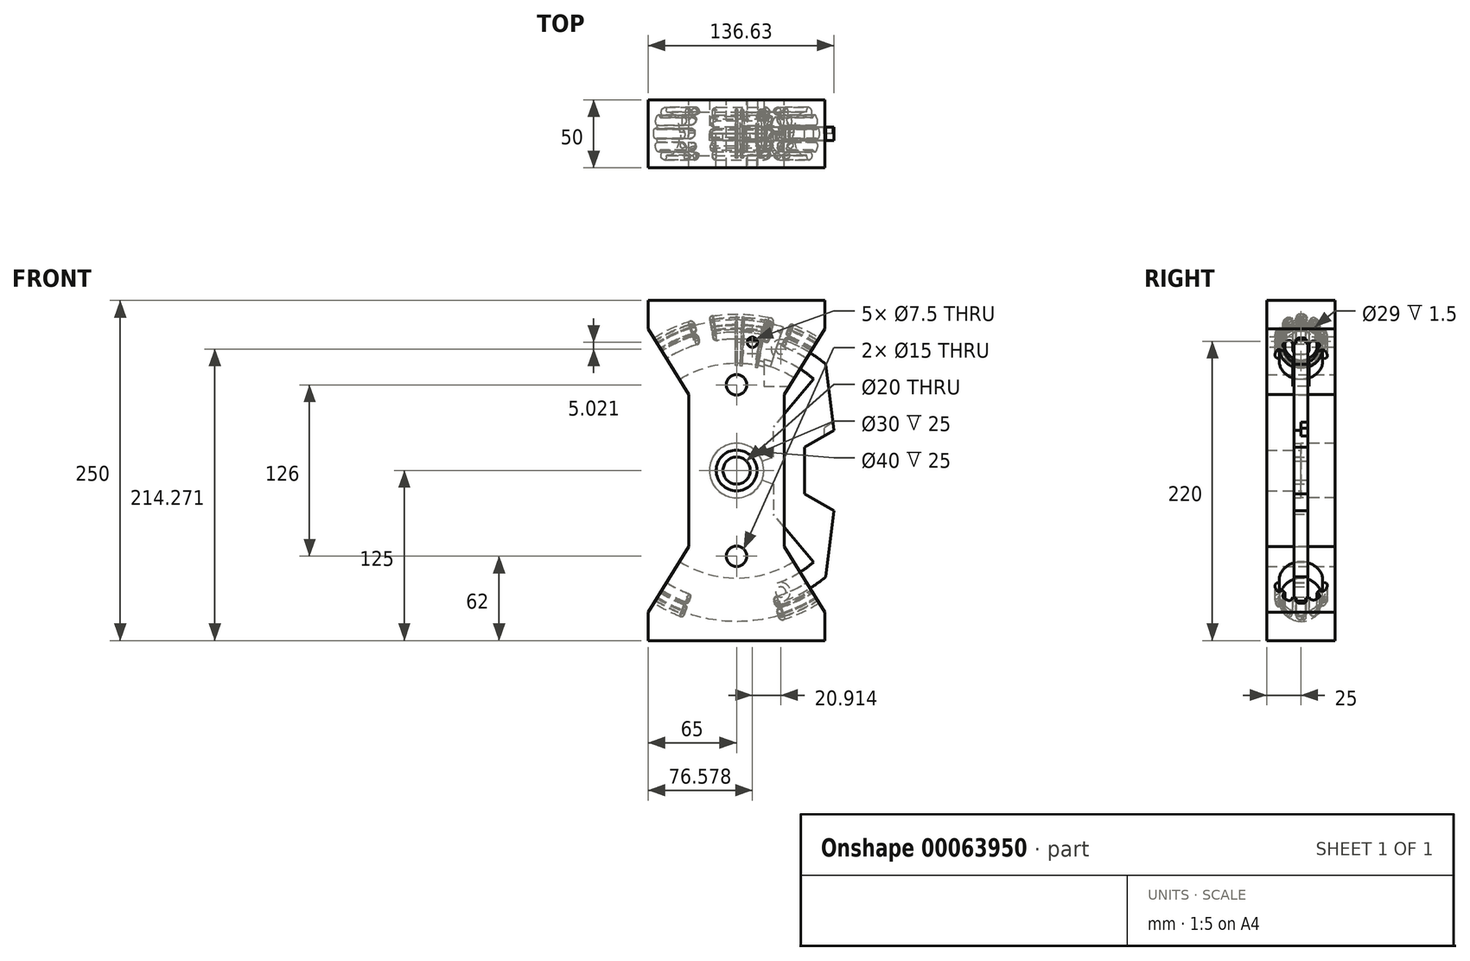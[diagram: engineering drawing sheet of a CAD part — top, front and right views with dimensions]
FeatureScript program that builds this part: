
annotation { "Feature Type Name" : "Feature", "Feature Type Description" : "" }
export const myFeature = defineFeature(function(context is Context, id is Id, definition is map)
    precondition{}
    {
        {
            var Q0;
            Q0=qCreatedBy(makeId("Front.planeOp"),FACE);
            var sketch = newSketch(context, id + "F0", { "sketchPlane" : qUnion([Q0])});
            skCircle(sketch, "E0", {"center": v(0, 0) * mm, "radius": 95 * mm, "construction": true});
            skLineSegment(sketch, "E1", {"start": v(0, 95) * mm, "end": v(0, 0) * mm, "construction": true});
            skLineSegment(sketch, "E2", {"start": v(0, 89.27) * mm, "end": v(32.5, 89.27) * mm, "construction": true});
            skLineSegment(sketch, "E3", {"start": v(0, 0) * mm, "end": v(32.5, 89.27) * mm, "construction": true});
            skLineSegment(sketch, "E4", {"start": v(0, 95) * mm, "end": v(0, 89.27) * mm});
            skLineSegment(sketch, "E5", {"start": v(0, -95) * mm, "end": v(0, -79) * mm});
            skCircle(sketch, "E6", {"center": v(0, 0) * mm, "radius": 79 * mm});
            skLineSegment(sketch, "E7", {"start": v(0, -95) * mm, "end": v(0, -111) * mm});
            skCircle(sketch, "E8", {"center": v(0, 0) * mm, "radius": 111 * mm});
            skLineSegment(sketch, "E9.rect.bottom", {"start": v(65, 125) * mm, "end": v(-65, 125) * mm});
            skLineSegment(sketch, "E9.rect.top", {"start": v(65, -125) * mm, "end": v(-65, -125) * mm});
            skLineSegment(sketch, "E9.rect.left", {"start": v(65, 125) * mm, "end": v(65, -125) * mm});
            skLineSegment(sketch, "E9.rect.right", {"start": v(-65, 125) * mm, "end": v(-65, -125) * mm});
            skCircle(sketch, "E10", {"center": v(0, 0) * mm, "radius": 15 * mm});
            skLineSegment(sketch, "E11", {"start": v(0, 0) * mm, "end": v(65, 104.02) * mm});
            skLineSegment(sketch, "E12", {"start": v(0, 0) * mm, "end": v(143.52, 0) * mm, "construction": true});
            skLineSegment(sketch, "E13", {"start": v(35, 56.01) * mm, "end": v(35, 0) * mm});
            skLineSegment(sketch, "E14", {"start": v(0, 95) * mm, "end": v(32.5, 89.27) * mm, "construction": true});
            skLineSegment(sketch, "E15.MirrorCS", {"start": v(35, -56.01) * mm, "end": v(35, 0) * mm});
            skLineSegment(sketch, "E16.MirrorCS", {"start": v(0, 0) * mm, "end": v(65, -104.02) * mm});
            skLineSegment(sketch, "E17.MirrorCS", {"start": v(0, 0) * mm, "end": v(-65, 104.02) * mm});
            skLineSegment(sketch, "E18.MirrorCS", {"start": v(-35, 56.01) * mm, "end": v(-35, 0) * mm});
            skLineSegment(sketch, "E19.MirrorCS", {"start": v(-35, -56.01) * mm, "end": v(-35, 0) * mm});
            skLineSegment(sketch, "E20.MirrorCS", {"start": v(0, 0) * mm, "end": v(-65, -104.02) * mm});
            skPoint(sketch, "E21", {"position": v(0, 79) * mm});
            skCircle(sketch, "E22", {"center": v(0, 95) * mm, "radius": 16 * mm, "construction": true});
            skLineSegment(sketch, "E23", {"start": v(0, 95) * mm, "end": v(-57.96, 79.47) * mm, "construction": true});
            skLineSegment(sketch, "E24", {"start": v(-14.07, 102.62) * mm, "end": v(-60.8, 90.1) * mm, "construction": true});
            skLineSegment(sketch, "E25", {"start": v(-60.8, 90.1) * mm, "end": v(-57.96, 79.47) * mm, "construction": true});
            skLineSegment(sketch, "E26.MirrorCS", {"start": v(-8.38, 81.37) * mm, "end": v(-55.1, 68.85) * mm, "construction": true});
            skLineSegment(sketch, "E27.MirrorCS", {"start": v(-55.1, 68.85) * mm, "end": v(-57.96, 79.47) * mm, "construction": true});
            skCircle(sketch, "E28", {"center": v(0, 63) * mm, "radius": 7.5 * mm});
            skCircle(sketch, "E29.MirrorC", {"center": v(0, -63) * mm, "radius": 7.5 * mm});
            skSolve(sketch);
        }
        {
            var Q0;
            {var subQ1=sQuery(id+"F0.wireOp",EDGE,"E9.rect.bottom");Q0=makeQuery(id+"F0.imprint","IMPRINT",FACE,{"disambiguationData":[TD([[makeQuery(id+"F0.imprint","IMPRINT",EDGE,{"derivedFrom":subQ1}),1.0]])]});}
            var Q1;
            {var subQ1=sQuery(id+"F0.wireOp",EDGE,"E9.rect.top");Q1=makeQuery(id+"F0.imprint","IMPRINT",FACE,{"disambiguationData":[TD([[makeQuery(id+"F0.imprint","IMPRINT",EDGE,{"derivedFrom":subQ1}),-1.0]])]});}
            var Q2;
            {var subQ0=sQuery(id+"F0.wireOp",EDGE,"E11");var subQ1=sQuery(id+"F0.wireOp",EDGE,"E6");var subQ2=makeQuery(id+"F0.imprint","INTERSECT",VERTEX,{"derivedFrom":[subQ1,subQ0]});Q2=makeQuery(id+"F0.imprint","IMPRINT",FACE,{"disambiguationData":[TD([[makeQuery(id+"F0.imprint","IMPRINT",EDGE,{"disambiguationData":[TD([[subQ2,-1.0]])],"derivedFrom":subQ1}),-1.0]])]});}
            var Q3;
            {var subQ0=sQuery(id+"F0.wireOp",EDGE,"E11");var subQ2=sQuery(id+"F0.wireOp",EDGE,"E6");var subQ3=makeQuery(id+"F0.imprint","INTERSECT",VERTEX,{"derivedFrom":[subQ2,subQ0]});Q3=makeQuery(id+"F0.imprint","IMPRINT",FACE,{"disambiguationData":[TD([[makeQuery(id+"F0.imprint","IMPRINT",EDGE,{"disambiguationData":[TD([[subQ3,-1.0]])],"derivedFrom":subQ2}),1.0]])]});}
            var Q4;
            {var subQ1=sQuery(id+"F0.wireOp",EDGE,"E18.MirrorCS");Q4=makeQuery(id+"F0.imprint","IMPRINT",FACE,{"disambiguationData":[TD([[makeQuery(id+"F0.imprint","IMPRINT",EDGE,{"derivedFrom":subQ1}),1.0]])]});}
            var Q5;
            {var subQ1=sQuery(id+"F0.wireOp",EDGE,"E13");Q5=makeQuery(id+"F0.imprint","IMPRINT",FACE,{"disambiguationData":[TD([[makeQuery(id+"F0.imprint","IMPRINT",EDGE,{"derivedFrom":subQ1}),-1.0]])]});}
            var Q6;
            {var subQ2=sQuery(id+"F0.wireOp",EDGE,"E5");Q6=makeQuery(id+"F0.imprint","IMPRINT",FACE,{"disambiguationData":[TD([[makeQuery(id+"F0.imprint","IMPRINT",EDGE,{"derivedFrom":subQ2}),-1.0]])]});}
            var Q7;
            {var subQ2=sQuery(id+"F0.wireOp",EDGE,"E5");Q7=makeQuery(id+"F0.imprint","IMPRINT",FACE,{"disambiguationData":[TD([[makeQuery(id+"F0.imprint","IMPRINT",EDGE,{"derivedFrom":subQ2}),1.0]])]});}
            var Q8;
            {var subQ6=sQuery(id+"F0.wireOp",EDGE,"E6");var subQ7=makeQuery(id+"F0.imprint","INTERSECT",VERTEX,{"derivedFrom":[sQuery(id+"F0.wireOp",EDGE,"E5"),subQ6]});Q8=makeQuery(id+"F0.imprint","IMPRINT",FACE,{"disambiguationData":[TD([[makeQuery(id+"F0.imprint","IMPRINT",EDGE,{"disambiguationData":[TD([[subQ7,1.0]])],"derivedFrom":subQ6}),1.0]])]});}
            extrude(context, id + "F1", {"entities" : qUnion([Q0, Q1, Q2, Q3, Q4, Q5, Q6, Q7, Q8]), "endBound" : BoundingType.SYMMETRIC, "depth" : 50 * mm});
        }
        {
            var Q0;
            Q0=qCreatedBy(makeId("Right.planeOp"),FACE);
            var sketch = newSketch(context, id + "F2", { "sketchPlane" : qUnion([Q0])});
            skCircle(sketch, "E30", {"center": v(0, 95) * mm, "radius": 16 * mm});
            skLineSegment(sketch, "E31", {"start": v(-6, 80.17) * mm, "end": v(-6, 0) * mm});
            skLineSegment(sketch, "E32", {"start": v(-6, 0) * mm, "end": v(0, 0) * mm});
            skLineSegment(sketch, "E33", {"start": v(0, 0) * mm, "end": v(6, 0) * mm});
            skLineSegment(sketch, "E34", {"start": v(6, 0) * mm, "end": v(6, 80.17) * mm});
            skLineSegment(sketch, "E35", {"start": v(-6, 0) * mm, "end": v(-85.58, 0) * mm});
            skSolve(sketch);
        }
        {
            var Q0;
            {var subQ0=sQuery(id+"F2.wireOp",EDGE,"E30");var subQ1=makeQuery(id+"F2.imprint","INTERSECT",VERTEX,{"derivedFrom":[subQ0,sQuery(id+"F2.wireOp",EDGE,"E31")]});Q0=makeQuery(id+"F2.imprint","IMPRINT",FACE,{"disambiguationData":[TD([[makeQuery(id+"F2.imprint","IMPRINT",EDGE,{"disambiguationData":[TD([[subQ1,-1.0]])],"derivedFrom":subQ0}),1.0]])]});}
            var Q1;
            Q1=sQuery(id+"F2.wireOp",EDGE,"E35");
            revolve(context, id + "F3", {"operationType" : NewBodyOperationType.REMOVE, "entities" : qUnion([Q0]), "axis" : qUnion([Q1]), "revolveType" : RevolveType.FULL, "oppositeDirection" : true});
        }
        {
            var Q0;
            Q0=qCreatedBy(makeId("Right.planeOp"),FACE);
            var sketch = newSketch(context, id + "F4", { "sketchPlane" : qUnion([Q0])});
            skCircle(sketch, "E36", {"center": v(0, 95) * mm, "radius": 15.98 * mm});
            skSolve(sketch);
        }
        {
            var Q0;
            Q0=qSketchRegion(id+"F4",true);
            var Q1;
            Q1=sQuery(id+"F2.wireOp",EDGE,"E35");
            revolve(context, id + "F5", {"entities" : qUnion([Q0]), "axis" : qUnion([Q1]), "revolveType" : RevolveType.ONE_DIRECTION, "oppositeDirection" : true, "angle" : 18 * degree});
        }
        {
            var Q0;
            Q0=qCreatedBy(makeId("Front.planeOp"),FACE);
            var sketch = newSketch(context, id + "F6", { "sketchPlane" : qUnion([Q0])});
            skLineSegment(sketch, "E37", {"start": v(0, 0) * mm, "end": v(0, 138.47) * mm});
            skLineSegment(sketch, "E38", {"start": v(0, 0) * mm, "end": v(11.58, 94.3) * mm});
            skCircle(sketch, "E39", {"center": v(11.58, 94.3) * mm, "radius": 3.75 * mm});
            skLineSegment(sketch, "E40", {"start": v(0, 0) * mm, "end": v(37.76, 116.21) * mm});
            skCircle(sketch, "E41", {"center": v(11.58, 94.3) * mm, "radius": 6.14 * mm});
            skLineSegment(sketch, "E42.bottom", {"start": v(20.13, 102.54) * mm, "end": v(41.82, 102.54) * mm});
            skLineSegment(sketch, "E42.top", {"start": v(20.13, 61.74) * mm, "end": v(41.82, 61.74) * mm});
            skLineSegment(sketch, "E42.left", {"start": v(20.13, 102.54) * mm, "end": v(20.13, 61.74) * mm});
            skLineSegment(sketch, "E42.right", {"start": v(41.82, 102.54) * mm, "end": v(41.82, 61.74) * mm});
            skLineSegment(sketch, "E43.bottom", {"start": v(20.13, 102.54) * mm, "end": v(5.32, 102.54) * mm});
            skLineSegment(sketch, "E43.top", {"start": v(20.13, 85.67) * mm, "end": v(5.32, 85.67) * mm});
            skLineSegment(sketch, "E43.left", {"start": v(20.13, 102.54) * mm, "end": v(20.13, 85.67) * mm});
            skLineSegment(sketch, "E43.right", {"start": v(5.32, 102.54) * mm, "end": v(5.32, 85.67) * mm});
            skSolve(sketch);
        }
        {
            var Q0;
            {var subQ5=sQuery(id+"F6.wireOp",EDGE,"E42.right");Q0=makeQuery(id+"F6.imprint","IMPRINT",FACE,{"disambiguationData":[TD([[makeQuery(id+"F6.imprint","IMPRINT",EDGE,{"derivedFrom":subQ5}),-1.0]])]});}
            var Q1;
            {var subQ0=sQuery(id+"F6.wireOp",EDGE,"E42.left");Q1=makeQuery(id+"F6.imprint","IMPRINT",FACE,{"disambiguationData":[TD([[makeQuery(id+"F6.imprint","IMPRINT",EDGE,{"derivedFrom":subQ0}),1.0]])]});}
            var Q2;
            Q2=makeQuery(id+"F6.imprint","IMPRINT",FACE,{"disambiguationData":[TD([[makeQuery(id+"F6.imprint","IMPRINT",EDGE,{"derivedFrom":sQuery(id+"F6.wireOp",EDGE,"E41")}),-1.0]])]});
            var Q3;
            Q3=makeQuery(id+"F6.imprint","IMPRINT",FACE,{"disambiguationData":[TD([[makeQuery(id+"F6.imprint","IMPRINT",EDGE,{"derivedFrom":sQuery(id+"F6.wireOp",EDGE,"E39")}),-1.0]])]});
            var Q4;
            Q4=makeQuery(id+"F6.imprint","IMPRINT",FACE,{"disambiguationData":[TD([[makeQuery(id+"F6.imprint","IMPRINT",EDGE,{"derivedFrom":sQuery(id+"F6.wireOp",EDGE,"E39")}),1.0]])]});
            extrude(context, id + "F7", {"entities" : qUnion([Q0, Q1, Q2, Q3, Q4]), "operationType" : NewBodyOperationType.REMOVE, "endBound" : BoundingType.SYMMETRIC, "oppositeDirection" : true, "depth" : 12 * mm});
        }
        {
            var Q0;
            Q0=makeQuery(id+"F7.boolean.opBoolean","COPY",EDGE,{"derivedFrom":makeQuery(id+"F7.opExtrude","CAP_EDGE",EDGE,{"disambiguationData":[OSD([sQuery(id+"F6.wireOp",EDGE,"E42.bottom"),sQuery(id+"F6.wireOp",EDGE,"E43.bottom")])],"isStart":false})});
            var Q1;
            Q1=makeQuery(id+"F7.boolean.opBoolean","COPY",EDGE,{"derivedFrom":makeQuery(id+"F7.opExtrude","CAP_EDGE",EDGE,{"disambiguationData":[OSD([sQuery(id+"F6.wireOp",EDGE,"E42.bottom"),sQuery(id+"F6.wireOp",EDGE,"E43.bottom")])],"isStart":true})});
            var Q2;
            Q2=makeQuery(id+"F7.boolean.opBoolean","COPY",EDGE,{"derivedFrom":makeQuery(id+"F7.opExtrude","CAP_EDGE",EDGE,{"disambiguationData":[OSD([sQuery(id+"F6.wireOp",EDGE,"E43.top")])],"isStart":false})});
            var Q3;
            Q3=makeQuery(id+"F7.boolean.opBoolean","COPY",EDGE,{"derivedFrom":makeQuery(id+"F7.opExtrude","CAP_EDGE",EDGE,{"disambiguationData":[OSD([sQuery(id+"F6.wireOp",EDGE,"E43.top")])],"isStart":true})});
            fillet(context, id + "F8", {"entities" : qUnion([Q0, Q1, Q2, Q3]), "radius" : 3 * mm, "allowEdgeOverflow" : false});
        }
        {
            var Q0;
            Q0=makeQuery(id+"F6.imprint","IMPRINT",FACE,{"disambiguationData":[TD([[makeQuery(id+"F6.imprint","IMPRINT",EDGE,{"derivedFrom":sQuery(id+"F6.wireOp",EDGE,"E39")}),1.0]])]});
            extrude(context, id + "F9", {"entities" : qUnion([Q0]), "operationType" : NewBodyOperationType.REMOVE, "endBound" : BoundingType.SYMMETRIC, "oppositeDirection" : true, "depth" : 50 * mm});
        }
        {
            var Q0;
            Q0=qCreatedBy(makeId("Right.planeOp"),FACE);
            var sketch = newSketch(context, id + "F10", { "sketchPlane" : qUnion([Q0])});
            skCircle(sketch, "E44", {"center": v(0, 95) * mm, "radius": 12.5 * mm});
            skSolve(sketch);
        }
        {
            var Q0;
            Q0=qSketchRegion(id+"F10",true);
            var Q1;
            Q1=sQuery(id+"F2.wireOp",EDGE,"E35");
            revolve(context, id + "F11", {"operationType" : NewBodyOperationType.REMOVE, "entities" : qUnion([Q0]), "axis" : qUnion([Q1]), "revolveType" : RevolveType.TWO_DIRECTIONS, "oppositeDirection" : true, "angle" : 30 * degree, "angleBack" : 10 * degree});
        }
        {
            var Q0;
            Q0=qCreatedBy(makeId("Right.planeOp"),FACE);
            var sketch = newSketch(context, id + "F12", { "sketchPlane" : qUnion([Q0])});
            skCircle(sketch, "E45", {"center": v(0, 95) * mm, "radius": 14.5 * mm});
            skCircle(sketch, "E46", {"center": v(0, 95) * mm, "radius": 18 * mm});
            skSolve(sketch);
        }
        {
            var Q0;
            Q0=qSketchRegion(id+"F12",true);
            extrude(context, id + "F13", {"entities" : qUnion([Q0]), "endBound" : BoundingType.SYMMETRIC, "depth" : 1.5 * mm});
        }
        {
            var Q0;
            Q0=makeQuery(id+"F13.opExtrude","SWEPT_BODY",BODY,{"disambiguationData":[OSD([sQuery(id+"F12.wireOp",EDGE,"E45"),sQuery(id+"F12.wireOp",EDGE,"E46")])]});
            var Q1;
            Q1=sQuery(id+"F2.wireOp",EDGE,"E35");
            transform(context, id + "F14", {"entities" : qUnion([Q0]), "transformType" : TransformType.ROTATION, "transformAxis" : qUnion([Q1]), "angle" : 2.5 * degree, "oppositeDirection" : true, "makeCopy" : true});
        }
        {
            var Q0;
            Q0=makeQuery(id+"F13.opExtrude","SWEPT_BODY",BODY,{"disambiguationData":[OSD([sQuery(id+"F12.wireOp",EDGE,"E45"),sQuery(id+"F12.wireOp",EDGE,"E46")])]});
            var Q1;
            Q1=sQuery(id+"F2.wireOp",EDGE,"E35");
            transform(context, id + "F15", {"entities" : qUnion([Q0]), "transformType" : TransformType.ROTATION, "transformAxis" : qUnion([Q1]), "angle" : 11 * degree, "oppositeDirection" : true, "makeCopy" : true});
        }
        {
            var Q0;
            Q0=makeQuery(id+"F14.opPattern","COPY",BODY,{"derivedFrom":makeQuery(id+"F13.opExtrude","SWEPT_BODY",BODY,{"disambiguationData":[OSD([sQuery(id+"F12.wireOp",EDGE,"E45"),sQuery(id+"F12.wireOp",EDGE,"E46")])]}),"instanceName":"1"});
            var Q1;
            Q1=makeQuery(id+"F15.opPattern","COPY",BODY,{"derivedFrom":makeQuery(id+"F13.opExtrude","SWEPT_BODY",BODY,{"disambiguationData":[OSD([sQuery(id+"F12.wireOp",EDGE,"E45"),sQuery(id+"F12.wireOp",EDGE,"E46")])]}),"instanceName":"1"});
            var Q2;
            Q2=makeQuery(id+"F5.opRevolve","SWEPT_BODY",BODY,{"disambiguationData":[OSD([sQuery(id+"F4.wireOp",EDGE,"E36")])]});
            booleanBodies(context, id + "F16", {"operationType" : BooleanOperationType.SUBTRACTION, "tools" : qUnion([Q0, Q1]), "targets" : qUnion([Q2]), "keepTools" : true});
        }
        {
            var Q0;
            Q0=qCreatedBy(makeId("Front.planeOp"),FACE);
            var sketch = newSketch(context, id + "F17", { "sketchPlane" : qUnion([Q0])});
            skCircle(sketch, "E47", {"center": v(0, 0) * mm, "radius": 20 * mm});
            skLineSegment(sketch, "E48", {"start": v(0, 0) * mm, "end": v(27, 9.83) * mm});
            skLineSegment(sketch, "E49", {"start": v(0, 0) * mm, "end": v(-52.85, 0) * mm});
            skLineSegment(sketch, "E50", {"start": v(0, 0) * mm, "end": v(32.5, 89.27) * mm, "construction": true});
            skCircle(sketch, "E51", {"center": v(32.5, 89.27) * mm, "radius": 7 * mm});
            skCircle(sketch, "E52", {"center": v(32.5, 89.27) * mm, "radius": 3.75 * mm});
            skArc(sketch, "E53", {"start": v(56.57, 67.41) * mm, "mid": v(44, 76.21) * mm, "end": v(30.1, 82.7) * mm});
            skArc(sketch, "E54", {"start": v(65.56, 78.14) * mm, "mid": v(51, 88.33) * mm, "end": v(34.89, 95.85) * mm});
            skLineSegment(sketch, "E55", {"start": v(56.57, 67.41) * mm, "end": v(0, 0) * mm});
            skLineSegment(sketch, "E56", {"start": v(56.57, 67.41) * mm, "end": v(65.56, 78.14) * mm});
            skLineSegment(sketch, "E57", {"start": v(27, 9.83) * mm, "end": v(27, 32.18) * mm});
            skLineSegment(sketch, "E58", {"start": v(65.56, 78.14) * mm, "end": v(71.63, 29.58) * mm});
            skLineSegment(sketch, "E59", {"start": v(71.63, 29.58) * mm, "end": v(50, 17.1) * mm});
            skLineSegment(sketch, "E60", {"start": v(50, 17.1) * mm, "end": v(50, 0) * mm});
            skLineSegment(sketch, "E61.MirrorCS", {"start": v(0, 0) * mm, "end": v(32.5, -89.27) * mm, "construction": true});
            skLineSegment(sketch, "E62.MirrorCS", {"start": v(56.57, -67.41) * mm, "end": v(0, 0) * mm});
            skArc(sketch, "E63.MirrorCS", {"start": v(56.57, -67.41) * mm, "mid": v(44, -76.21) * mm, "end": v(30.1, -82.7) * mm});
            skCircle(sketch, "E64.MirrorC", {"center": v(32.5, -89.27) * mm, "radius": 7 * mm});
            skCircle(sketch, "E65.MirrorC", {"center": v(32.5, -89.27) * mm, "radius": 3.75 * mm});
            skArc(sketch, "E66.MirrorCS", {"start": v(65.56, -78.14) * mm, "mid": v(51, -88.33) * mm, "end": v(34.89, -95.85) * mm});
            skLineSegment(sketch, "E67.MirrorCS", {"start": v(65.56, -78.14) * mm, "end": v(71.63, -29.58) * mm});
            skLineSegment(sketch, "E68.MirrorCS", {"start": v(71.63, -29.58) * mm, "end": v(50, -17.1) * mm});
            skLineSegment(sketch, "E69.MirrorCS", {"start": v(50, -17.1) * mm, "end": v(50, 0) * mm});
            skLineSegment(sketch, "E70.MirrorCS", {"start": v(27, -9.83) * mm, "end": v(27, -32.18) * mm});
            skLineSegment(sketch, "E71.MirrorCS", {"start": v(0, 0) * mm, "end": v(27, -9.83) * mm});
            skCircle(sketch, "E72", {"center": v(0, 0) * mm, "radius": 10 * mm});
            skSolve(sketch);
        }
        {
            var Q0;
            Q0=makeQuery(id+"F17.imprint","IMPRINT",FACE,{"disambiguationData":[TD([[makeQuery(id+"F17.imprint","IMPRINT",EDGE,{"derivedFrom":sQuery(id+"F17.wireOp",EDGE,"E52")}),-1.0]])]});
            var Q1;
            {var subQ0=sQuery(id+"F17.wireOp",EDGE,"E53");Q1=makeQuery(id+"F17.imprint","IMPRINT",FACE,{"disambiguationData":[TD([[makeQuery(id+"F17.imprint","IMPRINT",EDGE,{"derivedFrom":subQ0}),-1.0]])]});}
            var Q2;
            {var subQ9=sQuery(id+"F17.wireOp",EDGE,"E56");Q2=makeQuery(id+"F17.imprint","IMPRINT",FACE,{"disambiguationData":[TD([[makeQuery(id+"F17.imprint","IMPRINT",EDGE,{"derivedFrom":subQ9}),-1.0]])]});}
            var Q3;
            {var subQ0=sQuery(id+"F17.wireOp",EDGE,"E48");var subQ1=sQuery(id+"F17.wireOp",EDGE,"E47");var subQ2=makeQuery(id+"F17.imprint","INTERSECT",VERTEX,{"derivedFrom":[subQ1,subQ0]});Q3=makeQuery(id+"F17.imprint","IMPRINT",FACE,{"disambiguationData":[TD([[makeQuery(id+"F17.imprint","IMPRINT",EDGE,{"disambiguationData":[TD([[subQ2,1.0]])],"derivedFrom":subQ1}),1.0]])]});}
            var Q4;
            {var subQ0=sQuery(id+"F17.wireOp",EDGE,"E49");var subQ1=sQuery(id+"F17.wireOp",EDGE,"E47");var subQ2=makeQuery(id+"F17.imprint","INTERSECT",VERTEX,{"derivedFrom":[subQ1,subQ0]});Q4=makeQuery(id+"F17.imprint","IMPRINT",FACE,{"disambiguationData":[TD([[makeQuery(id+"F17.imprint","IMPRINT",EDGE,{"disambiguationData":[TD([[subQ2,1.0]])],"derivedFrom":subQ1}),1.0]])]});}
            var Q5;
            {var subQ0=sQuery(id+"F17.wireOp",EDGE,"E55");var subQ1=sQuery(id+"F17.wireOp",EDGE,"E47");var subQ2=makeQuery(id+"F17.imprint","INTERSECT",VERTEX,{"derivedFrom":[subQ1,subQ0]});Q5=makeQuery(id+"F17.imprint","IMPRINT",FACE,{"disambiguationData":[TD([[makeQuery(id+"F17.imprint","IMPRINT",EDGE,{"disambiguationData":[TD([[subQ2,1.0]])],"derivedFrom":subQ1}),1.0]])]});}
            var Q6;
            {var subQ0=sQuery(id+"F17.wireOp",EDGE,"E62.MirrorCS");var subQ1=sQuery(id+"F17.wireOp",EDGE,"E47");var subQ2=makeQuery(id+"F17.imprint","INTERSECT",VERTEX,{"derivedFrom":[subQ1,subQ0]});Q6=makeQuery(id+"F17.imprint","IMPRINT",FACE,{"disambiguationData":[TD([[makeQuery(id+"F17.imprint","IMPRINT",EDGE,{"disambiguationData":[TD([[subQ2,-1.0]])],"derivedFrom":subQ1}),1.0]])]});}
            var Q7;
            {var subQ0=sQuery(id+"F17.wireOp",EDGE,"E49");var subQ1=sQuery(id+"F17.wireOp",EDGE,"E47");var subQ2=makeQuery(id+"F17.imprint","INTERSECT",VERTEX,{"derivedFrom":[subQ1,subQ0]});Q7=makeQuery(id+"F17.imprint","IMPRINT",FACE,{"disambiguationData":[TD([[makeQuery(id+"F17.imprint","IMPRINT",EDGE,{"disambiguationData":[TD([[subQ2,-1.0]])],"derivedFrom":subQ1}),1.0]])]});}
            var Q8;
            Q8=makeQuery(id+"F17.imprint","IMPRINT",FACE,{"disambiguationData":[TD([[makeQuery(id+"F17.imprint","IMPRINT",EDGE,{"derivedFrom":sQuery(id+"F17.wireOp",EDGE,"E65.MirrorC")}),1.0]])]});
            extrude(context, id + "F18", {"entities" : qUnion([Q0, Q1, Q2, Q3, Q4, Q5, Q6, Q7, Q8]), "endBound" : BoundingType.SYMMETRIC, "depth" : 10 * mm});
        }
        {
            var Q0;
            {var subQ0=sQuery(id+"F17.wireOp",EDGE,"E49");var subQ1=sQuery(id+"F17.wireOp",EDGE,"E47");var subQ2=makeQuery(id+"F17.imprint","INTERSECT",VERTEX,{"derivedFrom":[subQ1,subQ0]});Q0=makeQuery(id+"F17.imprint","IMPRINT",FACE,{"disambiguationData":[TD([[makeQuery(id+"F17.imprint","IMPRINT",EDGE,{"disambiguationData":[TD([[subQ2,1.0]])],"derivedFrom":subQ1}),1.0]])]});}
            var Q1;
            {var subQ0=sQuery(id+"F17.wireOp",EDGE,"E55");var subQ1=sQuery(id+"F17.wireOp",EDGE,"E47");var subQ2=makeQuery(id+"F17.imprint","INTERSECT",VERTEX,{"derivedFrom":[subQ1,subQ0]});Q1=makeQuery(id+"F17.imprint","IMPRINT",FACE,{"disambiguationData":[TD([[makeQuery(id+"F17.imprint","IMPRINT",EDGE,{"disambiguationData":[TD([[subQ2,1.0]])],"derivedFrom":subQ1}),1.0]])]});}
            var Q2;
            {var subQ0=sQuery(id+"F17.wireOp",EDGE,"E48");var subQ1=sQuery(id+"F17.wireOp",EDGE,"E47");var subQ2=makeQuery(id+"F17.imprint","INTERSECT",VERTEX,{"derivedFrom":[subQ1,subQ0]});Q2=makeQuery(id+"F17.imprint","IMPRINT",FACE,{"disambiguationData":[TD([[makeQuery(id+"F17.imprint","IMPRINT",EDGE,{"disambiguationData":[TD([[subQ2,1.0]])],"derivedFrom":subQ1}),1.0]])]});}
            var Q3;
            {var subQ0=sQuery(id+"F17.wireOp",EDGE,"E62.MirrorCS");var subQ1=sQuery(id+"F17.wireOp",EDGE,"E47");var subQ2=makeQuery(id+"F17.imprint","INTERSECT",VERTEX,{"derivedFrom":[subQ1,subQ0]});Q3=makeQuery(id+"F17.imprint","IMPRINT",FACE,{"disambiguationData":[TD([[makeQuery(id+"F17.imprint","IMPRINT",EDGE,{"disambiguationData":[TD([[subQ2,-1.0]])],"derivedFrom":subQ1}),1.0]])]});}
            var Q4;
            {var subQ0=sQuery(id+"F17.wireOp",EDGE,"E49");var subQ1=sQuery(id+"F17.wireOp",EDGE,"E47");var subQ2=makeQuery(id+"F17.imprint","INTERSECT",VERTEX,{"derivedFrom":[subQ1,subQ0]});Q4=makeQuery(id+"F17.imprint","IMPRINT",FACE,{"disambiguationData":[TD([[makeQuery(id+"F17.imprint","IMPRINT",EDGE,{"disambiguationData":[TD([[subQ2,-1.0]])],"derivedFrom":subQ1}),1.0]])]});}
            extrude(context, id + "F19", {"entities" : qUnion([Q0, Q1, Q2, Q3, Q4]), "operationType" : NewBodyOperationType.REMOVE, "oppositeDirection" : true, "depth" : 25 * mm});
        }
        {
            var Q0;
            Q0=qCreatedBy(makeId("Right.planeOp"),FACE);
            var sketch = newSketch(context, id + "F20", { "sketchPlane" : qUnion([Q0])});
            skCircle(sketch, "E73", {"center": v(0, 95) * mm, "radius": 20 * mm});
            skCircle(sketch, "E74", {"center": v(0, 95) * mm, "radius": 12.5 * mm});
            skLineSegment(sketch, "E75", {"start": v(0, 95) * mm, "end": v(25.24, 95) * mm, "construction": true});
            skLineSegment(sketch, "E76", {"start": v(0, 95) * mm, "end": v(-4.33, 114.53) * mm});
            skLineSegment(sketch, "E77", {"start": v(0, 95) * mm, "end": v(-7.65, 113.48) * mm});
            skLineSegment(sketch, "E78", {"start": v(0, 95) * mm, "end": v(-14.75, 108.51) * mm});
            skLineSegment(sketch, "E79", {"start": v(0, 95) * mm, "end": v(-16.87, 105.75) * mm});
            skLineSegment(sketch, "E80", {"start": v(0, 95) * mm, "end": v(0, 124.51) * mm, "construction": true});
            skLineSegment(sketch, "E81", {"start": v(0, 95) * mm, "end": v(-19.83, 97.61) * mm});
            skLineSegment(sketch, "E82", {"start": v(-14.75, 108.51) * mm, "end": v(-7.65, 113.48) * mm, "construction": true});
            skLineSegment(sketch, "E83", {"start": v(-19.83, 97.61) * mm, "end": v(-16.87, 105.75) * mm, "construction": true});
            skPoint(sketch, "E84", {"position": v(-11.2, 111) * mm});
            skPoint(sketch, "E85", {"position": v(-18.35, 101.68) * mm});
            skLineSegment(sketch, "E86", {"start": v(0, 95) * mm, "end": v(-11.2, 111) * mm, "construction": true});
            skLineSegment(sketch, "E87", {"start": v(0, 95) * mm, "end": v(-18.35, 101.68) * mm, "construction": true});
            skLineSegment(sketch, "E88.MirrorCS", {"start": v(0, 95) * mm, "end": v(4.33, 114.53) * mm});
            skLineSegment(sketch, "E89.MirrorCS", {"start": v(0, 95) * mm, "end": v(7.65, 113.48) * mm});
            skLineSegment(sketch, "E90.MirrorCS", {"start": v(0, 95) * mm, "end": v(14.75, 108.51) * mm});
            skLineSegment(sketch, "E91.MirrorCS", {"start": v(0, 95) * mm, "end": v(16.87, 105.75) * mm});
            skLineSegment(sketch, "E92.MirrorCS", {"start": v(0, 95) * mm, "end": v(19.83, 97.61) * mm});
            skSolve(sketch);
        }
        {
            var Q0;
            {var subQ0=sQuery(id+"F20.wireOp",EDGE,"E79");var subQ1=sQuery(id+"F20.wireOp",EDGE,"E73");var subQ2=makeQuery(id+"F20.imprint","INTERSECT",VERTEX,{"derivedFrom":[subQ1,subQ0]});Q0=makeQuery(id+"F20.imprint","IMPRINT",FACE,{"disambiguationData":[TD([[makeQuery(id+"F20.imprint","IMPRINT",EDGE,{"disambiguationData":[TD([[subQ2,-1.0]])],"derivedFrom":subQ1}),1.0]])]});}
            var Q1;
            {var subQ0=sQuery(id+"F20.wireOp",EDGE,"E77");var subQ1=sQuery(id+"F20.wireOp",EDGE,"E73");var subQ2=makeQuery(id+"F20.imprint","INTERSECT",VERTEX,{"derivedFrom":[subQ1,subQ0]});Q1=makeQuery(id+"F20.imprint","IMPRINT",FACE,{"disambiguationData":[TD([[makeQuery(id+"F20.imprint","IMPRINT",EDGE,{"disambiguationData":[TD([[subQ2,-1.0]])],"derivedFrom":subQ1}),1.0]])]});}
            var Q2;
            {var subQ0=sQuery(id+"F20.wireOp",EDGE,"E76");var subQ1=sQuery(id+"F20.wireOp",EDGE,"E73");var subQ2=makeQuery(id+"F20.imprint","INTERSECT",VERTEX,{"derivedFrom":[subQ1,subQ0]});Q2=makeQuery(id+"F20.imprint","IMPRINT",FACE,{"disambiguationData":[TD([[makeQuery(id+"F20.imprint","IMPRINT",EDGE,{"disambiguationData":[TD([[subQ2,1.0]])],"derivedFrom":subQ1}),1.0]])]});}
            var Q3;
            {var subQ0=sQuery(id+"F20.wireOp",EDGE,"E89.MirrorCS");var subQ1=sQuery(id+"F20.wireOp",EDGE,"E73");var subQ2=makeQuery(id+"F20.imprint","INTERSECT",VERTEX,{"derivedFrom":[subQ1,subQ0]});Q3=makeQuery(id+"F20.imprint","IMPRINT",FACE,{"disambiguationData":[TD([[makeQuery(id+"F20.imprint","IMPRINT",EDGE,{"disambiguationData":[TD([[subQ2,1.0]])],"derivedFrom":subQ1}),1.0]])]});}
            var Q4;
            {var subQ0=sQuery(id+"F20.wireOp",EDGE,"E91.MirrorCS");var subQ1=sQuery(id+"F20.wireOp",EDGE,"E73");var subQ2=makeQuery(id+"F20.imprint","INTERSECT",VERTEX,{"derivedFrom":[subQ1,subQ0]});Q4=makeQuery(id+"F20.imprint","IMPRINT",FACE,{"disambiguationData":[TD([[makeQuery(id+"F20.imprint","IMPRINT",EDGE,{"disambiguationData":[TD([[subQ2,1.0]])],"derivedFrom":subQ1}),1.0]])]});}
            var Q5;
            Q5=sQuery(id+"F2.wireOp",EDGE,"E35");
            revolve(context, id + "F21", {"entities" : qUnion([Q0, Q1, Q2, Q3, Q4]), "axis" : qUnion([Q5]), "revolveType" : RevolveType.TWO_DIRECTIONS, "oppositeDirection" : true, "angle" : 14 * degree, "angleBack" : 350 * degree});
        }
        {
            var Q0;
            Q0=makeQuery(id+"F21.opRevolve","CAP_EDGE",EDGE,{"disambiguationData":[OSD([sQuery(id+"F20.wireOp",EDGE,"E81")])],"isStart":false});
            var Q1;
            Q1=makeQuery(id+"F21.opRevolve","CAP_EDGE",EDGE,{"disambiguationData":[OSD([sQuery(id+"F20.wireOp",EDGE,"E78")])],"isStart":false});
            var Q2;
            Q2=makeQuery(id+"F21.opRevolve","CAP_EDGE",EDGE,{"disambiguationData":[OSD([sQuery(id+"F20.wireOp",EDGE,"E76")])],"isStart":false});
            var Q3;
            Q3=makeQuery(id+"F21.opRevolve","CAP_EDGE",EDGE,{"disambiguationData":[OSD([sQuery(id+"F20.wireOp",EDGE,"E89.MirrorCS")])],"isStart":false});
            var Q4;
            Q4=makeQuery(id+"F21.opRevolve","CAP_EDGE",EDGE,{"disambiguationData":[OSD([sQuery(id+"F20.wireOp",EDGE,"E91.MirrorCS")])],"isStart":false});
            fillet(context, id + "F22", {"entities" : qUnion([Q0, Q1, Q2, Q3, Q4]), "radius" : 4 * mm, "tangentPropagation" : true, "allowEdgeOverflow" : false});
        }
        {
            var Q0;
            {var subQ0=sQuery(id+"F20.wireOp",EDGE,"E73");Q0=makeQuery(id+"F21.opRevolve","CAP_EDGE",EDGE,{"disambiguationData":[OSD([subQ0]),TDD([makeQuery(id+"F20.imprint","IMPRINT",EDGE,{"disambiguationData":[TD([[makeQuery(id+"F20.imprint","INTERSECT",VERTEX,{"derivedFrom":[subQ0,sQuery(id+"F20.wireOp",EDGE,"E79")]}),-1.0]])],"derivedFrom":subQ0})])],"isStart":false});}
            var Q1;
            {var subQ0=sQuery(id+"F20.wireOp",EDGE,"E73");var subQ1=sQuery(id+"F20.wireOp",EDGE,"E81");Q1=makeQuery(id+"F22.opFillet","BLEND_EDGE",EDGE,{"blendedFrom":[makeQuery(id+"F21.opRevolve","CAP_EDGE",EDGE,{"disambiguationData":[OSD([subQ1])],"isStart":false}),makeQuery(id+"F21.opRevolve","SWEPT_FACE",FACE,{"disambiguationData":[OSD([subQ0]),TDD([makeQuery(id+"F20.imprint","IMPRINT",EDGE,{"disambiguationData":[TD([[makeQuery(id+"F20.imprint","INTERSECT",VERTEX,{"derivedFrom":[subQ0,sQuery(id+"F20.wireOp",EDGE,"E79")]}),-1.0]])],"derivedFrom":subQ0})])]})],"blendedInto":[makeQuery(id+"F21.opRevolve","SWEPT_FACE",FACE,{"disambiguationData":[OSD([subQ0]),TDD([makeQuery(id+"F20.imprint","IMPRINT",EDGE,{"disambiguationData":[TD([[makeQuery(id+"F20.imprint","INTERSECT",VERTEX,{"derivedFrom":[subQ0,sQuery(id+"F20.wireOp",EDGE,"E79")]}),-1.0]])],"derivedFrom":subQ0})])]})]});}
            var Q2;
            {var subQ0=sQuery(id+"F20.wireOp",EDGE,"E73");Q2=makeQuery(id+"F21.opRevolve","CAP_EDGE",EDGE,{"disambiguationData":[OSD([subQ0]),TDD([makeQuery(id+"F20.imprint","IMPRINT",EDGE,{"disambiguationData":[TD([[makeQuery(id+"F20.imprint","INTERSECT",VERTEX,{"derivedFrom":[subQ0,sQuery(id+"F20.wireOp",EDGE,"E77")]}),-1.0]])],"derivedFrom":subQ0})])],"isStart":false});}
            var Q3;
            {var subQ0=sQuery(id+"F20.wireOp",EDGE,"E73");var subQ1=sQuery(id+"F20.wireOp",EDGE,"E78");Q3=makeQuery(id+"F22.opFillet","BLEND_EDGE",EDGE,{"blendedFrom":[makeQuery(id+"F21.opRevolve","CAP_EDGE",EDGE,{"disambiguationData":[OSD([subQ1])],"isStart":false}),makeQuery(id+"F21.opRevolve","SWEPT_FACE",FACE,{"disambiguationData":[OSD([subQ0]),TDD([makeQuery(id+"F20.imprint","IMPRINT",EDGE,{"disambiguationData":[TD([[makeQuery(id+"F20.imprint","INTERSECT",VERTEX,{"derivedFrom":[subQ0,sQuery(id+"F20.wireOp",EDGE,"E77")]}),-1.0]])],"derivedFrom":subQ0})])]})],"blendedInto":[makeQuery(id+"F21.opRevolve","SWEPT_FACE",FACE,{"disambiguationData":[OSD([subQ0]),TDD([makeQuery(id+"F20.imprint","IMPRINT",EDGE,{"disambiguationData":[TD([[makeQuery(id+"F20.imprint","INTERSECT",VERTEX,{"derivedFrom":[subQ0,sQuery(id+"F20.wireOp",EDGE,"E77")]}),-1.0]])],"derivedFrom":subQ0})])]})]});}
            var Q4;
            {var subQ0=sQuery(id+"F20.wireOp",EDGE,"E73");Q4=makeQuery(id+"F21.opRevolve","CAP_EDGE",EDGE,{"disambiguationData":[OSD([subQ0]),TDD([makeQuery(id+"F20.imprint","IMPRINT",EDGE,{"disambiguationData":[TD([[makeQuery(id+"F20.imprint","INTERSECT",VERTEX,{"derivedFrom":[subQ0,sQuery(id+"F20.wireOp",EDGE,"E76")]}),1.0]])],"derivedFrom":subQ0})])],"isStart":false});}
            var Q5;
            {var subQ0=sQuery(id+"F20.wireOp",EDGE,"E76");var subQ1=sQuery(id+"F20.wireOp",EDGE,"E73");Q5=makeQuery(id+"F22.opFillet","BLEND_EDGE",EDGE,{"blendedFrom":[makeQuery(id+"F21.opRevolve","CAP_EDGE",EDGE,{"disambiguationData":[OSD([subQ0])],"isStart":false}),makeQuery(id+"F21.opRevolve","SWEPT_FACE",FACE,{"disambiguationData":[OSD([subQ1]),TDD([makeQuery(id+"F20.imprint","IMPRINT",EDGE,{"disambiguationData":[TD([[makeQuery(id+"F20.imprint","INTERSECT",VERTEX,{"derivedFrom":[subQ1,subQ0]}),1.0]])],"derivedFrom":subQ1})])]})],"blendedInto":[makeQuery(id+"F21.opRevolve","SWEPT_FACE",FACE,{"disambiguationData":[OSD([subQ1]),TDD([makeQuery(id+"F20.imprint","IMPRINT",EDGE,{"disambiguationData":[TD([[makeQuery(id+"F20.imprint","INTERSECT",VERTEX,{"derivedFrom":[subQ1,subQ0]}),1.0]])],"derivedFrom":subQ1})])]})]});}
            var Q6;
            {var subQ0=sQuery(id+"F20.wireOp",EDGE,"E73");Q6=makeQuery(id+"F21.opRevolve","CAP_EDGE",EDGE,{"disambiguationData":[OSD([subQ0]),TDD([makeQuery(id+"F20.imprint","IMPRINT",EDGE,{"disambiguationData":[TD([[makeQuery(id+"F20.imprint","INTERSECT",VERTEX,{"derivedFrom":[subQ0,sQuery(id+"F20.wireOp",EDGE,"E89.MirrorCS")]}),1.0]])],"derivedFrom":subQ0})])],"isStart":false});}
            var Q7;
            {var subQ0=sQuery(id+"F20.wireOp",EDGE,"E89.MirrorCS");var subQ1=sQuery(id+"F20.wireOp",EDGE,"E73");Q7=makeQuery(id+"F22.opFillet","BLEND_EDGE",EDGE,{"blendedFrom":[makeQuery(id+"F21.opRevolve","CAP_EDGE",EDGE,{"disambiguationData":[OSD([subQ0])],"isStart":false}),makeQuery(id+"F21.opRevolve","SWEPT_FACE",FACE,{"disambiguationData":[OSD([subQ1]),TDD([makeQuery(id+"F20.imprint","IMPRINT",EDGE,{"disambiguationData":[TD([[makeQuery(id+"F20.imprint","INTERSECT",VERTEX,{"derivedFrom":[subQ1,subQ0]}),1.0]])],"derivedFrom":subQ1})])]})],"blendedInto":[makeQuery(id+"F21.opRevolve","SWEPT_FACE",FACE,{"disambiguationData":[OSD([subQ1]),TDD([makeQuery(id+"F20.imprint","IMPRINT",EDGE,{"disambiguationData":[TD([[makeQuery(id+"F20.imprint","INTERSECT",VERTEX,{"derivedFrom":[subQ1,subQ0]}),1.0]])],"derivedFrom":subQ1})])]})]});}
            var Q8;
            {var subQ0=sQuery(id+"F20.wireOp",EDGE,"E73");Q8=makeQuery(id+"F21.opRevolve","CAP_EDGE",EDGE,{"disambiguationData":[OSD([subQ0]),TDD([makeQuery(id+"F20.imprint","IMPRINT",EDGE,{"disambiguationData":[TD([[makeQuery(id+"F20.imprint","INTERSECT",VERTEX,{"derivedFrom":[subQ0,sQuery(id+"F20.wireOp",EDGE,"E91.MirrorCS")]}),1.0]])],"derivedFrom":subQ0})])],"isStart":false});}
            var Q9;
            {var subQ0=sQuery(id+"F20.wireOp",EDGE,"E91.MirrorCS");var subQ1=sQuery(id+"F20.wireOp",EDGE,"E73");Q9=makeQuery(id+"F22.opFillet","BLEND_EDGE",EDGE,{"blendedFrom":[makeQuery(id+"F21.opRevolve","CAP_EDGE",EDGE,{"disambiguationData":[OSD([subQ0])],"isStart":false}),makeQuery(id+"F21.opRevolve","SWEPT_FACE",FACE,{"disambiguationData":[OSD([subQ1]),TDD([makeQuery(id+"F20.imprint","IMPRINT",EDGE,{"disambiguationData":[TD([[makeQuery(id+"F20.imprint","INTERSECT",VERTEX,{"derivedFrom":[subQ1,subQ0]}),1.0]])],"derivedFrom":subQ1})])]})],"blendedInto":[makeQuery(id+"F21.opRevolve","SWEPT_FACE",FACE,{"disambiguationData":[OSD([subQ1]),TDD([makeQuery(id+"F20.imprint","IMPRINT",EDGE,{"disambiguationData":[TD([[makeQuery(id+"F20.imprint","INTERSECT",VERTEX,{"derivedFrom":[subQ1,subQ0]}),1.0]])],"derivedFrom":subQ1})])]})]});}
            fillet(context, id + "F23", {"entities" : qUnion([Q0, Q1, Q2, Q3, Q4, Q5, Q6, Q7, Q8, Q9]), "radius" : 3 * mm, "tangentPropagation" : true, "allowEdgeOverflow" : false});
        }
        {
            var Q0;
            Q0=makeQuery(id+"F21.opRevolve","CAP_EDGE",EDGE,{"disambiguationData":[OSD([sQuery(id+"F20.wireOp",EDGE,"E79")])],"isStart":true});
            var Q1;
            Q1=makeQuery(id+"F21.opRevolve","CAP_EDGE",EDGE,{"disambiguationData":[OSD([sQuery(id+"F20.wireOp",EDGE,"E77")])],"isStart":true});
            var Q2;
            Q2=makeQuery(id+"F21.opRevolve","CAP_EDGE",EDGE,{"disambiguationData":[OSD([sQuery(id+"F20.wireOp",EDGE,"E88.MirrorCS")])],"isStart":true});
            var Q3;
            Q3=makeQuery(id+"F21.opRevolve","CAP_EDGE",EDGE,{"disambiguationData":[OSD([sQuery(id+"F20.wireOp",EDGE,"E90.MirrorCS")])],"isStart":true});
            var Q4;
            Q4=makeQuery(id+"F21.opRevolve","CAP_EDGE",EDGE,{"disambiguationData":[OSD([sQuery(id+"F20.wireOp",EDGE,"E92.MirrorCS")])],"isStart":true});
            fillet(context, id + "F24", {"entities" : qUnion([Q0, Q1, Q2, Q3, Q4]), "radius" : 3 * mm, "tangentPropagation" : true, "allowEdgeOverflow" : false});
        }
        {
            var Q0;
            {var subQ0=sQuery(id+"F20.wireOp",EDGE,"E73");var subQ1=sQuery(id+"F20.wireOp",EDGE,"E88.MirrorCS");Q0=makeQuery(id+"F24.opFillet","BLEND_EDGE",EDGE,{"blendedFrom":[makeQuery(id+"F21.opRevolve","CAP_EDGE",EDGE,{"disambiguationData":[OSD([subQ1])],"isStart":true}),makeQuery(id+"F21.opRevolve","SWEPT_FACE",FACE,{"disambiguationData":[OSD([subQ0]),TDD([makeQuery(id+"F20.imprint","IMPRINT",EDGE,{"disambiguationData":[TD([[makeQuery(id+"F20.imprint","INTERSECT",VERTEX,{"derivedFrom":[subQ0,sQuery(id+"F20.wireOp",EDGE,"E76")]}),1.0]])],"derivedFrom":subQ0})])]})],"blendedInto":[makeQuery(id+"F21.opRevolve","SWEPT_FACE",FACE,{"disambiguationData":[OSD([subQ0]),TDD([makeQuery(id+"F20.imprint","IMPRINT",EDGE,{"disambiguationData":[TD([[makeQuery(id+"F20.imprint","INTERSECT",VERTEX,{"derivedFrom":[subQ0,sQuery(id+"F20.wireOp",EDGE,"E76")]}),1.0]])],"derivedFrom":subQ0})])]})]});}
            var Q1;
            {var subQ0=sQuery(id+"F20.wireOp",EDGE,"E76");var subQ1=sQuery(id+"F20.wireOp",EDGE,"E73");Q1=makeQuery(id+"F23.opFillet","BLEND_EDGE",EDGE,{"blendedFrom":[makeQuery(id+"F21.opRevolve","SWEPT_EDGE",EDGE,{"disambiguationData":[OSD([subQ1,subQ0])]}),makeQuery(id+"F21.opRevolve","CAP_FACE",FACE,{"disambiguationData":[OSD([subQ1,sQuery(id+"F20.wireOp",EDGE,"E74"),subQ0,sQuery(id+"F20.wireOp",EDGE,"E88.MirrorCS")])],"isStart":true})],"blendedInto":[makeQuery(id+"F21.opRevolve","CAP_FACE",FACE,{"disambiguationData":[OSD([subQ1,sQuery(id+"F20.wireOp",EDGE,"E74"),subQ0,sQuery(id+"F20.wireOp",EDGE,"E88.MirrorCS")])],"isStart":true})]});}
            var Q2;
            {var subQ0=sQuery(id+"F20.wireOp",EDGE,"E77");var subQ1=sQuery(id+"F20.wireOp",EDGE,"E73");Q2=makeQuery(id+"F24.opFillet","BLEND_EDGE",EDGE,{"blendedFrom":[makeQuery(id+"F21.opRevolve","CAP_EDGE",EDGE,{"disambiguationData":[OSD([subQ0])],"isStart":true}),makeQuery(id+"F21.opRevolve","SWEPT_FACE",FACE,{"disambiguationData":[OSD([subQ1]),TDD([makeQuery(id+"F20.imprint","IMPRINT",EDGE,{"disambiguationData":[TD([[makeQuery(id+"F20.imprint","INTERSECT",VERTEX,{"derivedFrom":[subQ1,subQ0]}),-1.0]])],"derivedFrom":subQ1})])]})],"blendedInto":[makeQuery(id+"F21.opRevolve","SWEPT_FACE",FACE,{"disambiguationData":[OSD([subQ1]),TDD([makeQuery(id+"F20.imprint","IMPRINT",EDGE,{"disambiguationData":[TD([[makeQuery(id+"F20.imprint","INTERSECT",VERTEX,{"derivedFrom":[subQ1,subQ0]}),-1.0]])],"derivedFrom":subQ1})])]})]});}
            var Q3;
            {var subQ0=sQuery(id+"F20.wireOp",EDGE,"E78");var subQ1=sQuery(id+"F20.wireOp",EDGE,"E73");Q3=makeQuery(id+"F23.opFillet","BLEND_EDGE",EDGE,{"blendedFrom":[makeQuery(id+"F21.opRevolve","SWEPT_EDGE",EDGE,{"disambiguationData":[OSD([subQ1,subQ0])]}),makeQuery(id+"F21.opRevolve","CAP_FACE",FACE,{"disambiguationData":[OSD([subQ1,sQuery(id+"F20.wireOp",EDGE,"E74"),sQuery(id+"F20.wireOp",EDGE,"E77"),subQ0])],"isStart":true})],"blendedInto":[makeQuery(id+"F21.opRevolve","CAP_FACE",FACE,{"disambiguationData":[OSD([subQ1,sQuery(id+"F20.wireOp",EDGE,"E74"),sQuery(id+"F20.wireOp",EDGE,"E77"),subQ0])],"isStart":true})]});}
            var Q4;
            {var subQ0=sQuery(id+"F20.wireOp",EDGE,"E79");var subQ1=sQuery(id+"F20.wireOp",EDGE,"E73");Q4=makeQuery(id+"F24.opFillet","BLEND_EDGE",EDGE,{"blendedFrom":[makeQuery(id+"F21.opRevolve","CAP_EDGE",EDGE,{"disambiguationData":[OSD([subQ0])],"isStart":true}),makeQuery(id+"F21.opRevolve","SWEPT_FACE",FACE,{"disambiguationData":[OSD([subQ1]),TDD([makeQuery(id+"F20.imprint","IMPRINT",EDGE,{"disambiguationData":[TD([[makeQuery(id+"F20.imprint","INTERSECT",VERTEX,{"derivedFrom":[subQ1,subQ0]}),-1.0]])],"derivedFrom":subQ1})])]})],"blendedInto":[makeQuery(id+"F21.opRevolve","SWEPT_FACE",FACE,{"disambiguationData":[OSD([subQ1]),TDD([makeQuery(id+"F20.imprint","IMPRINT",EDGE,{"disambiguationData":[TD([[makeQuery(id+"F20.imprint","INTERSECT",VERTEX,{"derivedFrom":[subQ1,subQ0]}),-1.0]])],"derivedFrom":subQ1})])]})]});}
            var Q5;
            {var subQ0=sQuery(id+"F20.wireOp",EDGE,"E81");var subQ1=sQuery(id+"F20.wireOp",EDGE,"E73");Q5=makeQuery(id+"F23.opFillet","BLEND_EDGE",EDGE,{"blendedFrom":[makeQuery(id+"F21.opRevolve","SWEPT_EDGE",EDGE,{"disambiguationData":[OSD([subQ1,subQ0])]}),makeQuery(id+"F21.opRevolve","CAP_FACE",FACE,{"disambiguationData":[OSD([subQ1,sQuery(id+"F20.wireOp",EDGE,"E74"),sQuery(id+"F20.wireOp",EDGE,"E79"),subQ0])],"isStart":true})],"blendedInto":[makeQuery(id+"F21.opRevolve","CAP_FACE",FACE,{"disambiguationData":[OSD([subQ1,sQuery(id+"F20.wireOp",EDGE,"E74"),sQuery(id+"F20.wireOp",EDGE,"E79"),subQ0])],"isStart":true})]});}
            var Q6;
            {var subQ0=sQuery(id+"F20.wireOp",EDGE,"E73");var subQ1=sQuery(id+"F20.wireOp",EDGE,"E90.MirrorCS");Q6=makeQuery(id+"F24.opFillet","BLEND_EDGE",EDGE,{"blendedFrom":[makeQuery(id+"F21.opRevolve","CAP_EDGE",EDGE,{"disambiguationData":[OSD([subQ1])],"isStart":true}),makeQuery(id+"F21.opRevolve","SWEPT_FACE",FACE,{"disambiguationData":[OSD([subQ0]),TDD([makeQuery(id+"F20.imprint","IMPRINT",EDGE,{"disambiguationData":[TD([[makeQuery(id+"F20.imprint","INTERSECT",VERTEX,{"derivedFrom":[subQ0,sQuery(id+"F20.wireOp",EDGE,"E89.MirrorCS")]}),1.0]])],"derivedFrom":subQ0})])]})],"blendedInto":[makeQuery(id+"F21.opRevolve","SWEPT_FACE",FACE,{"disambiguationData":[OSD([subQ0]),TDD([makeQuery(id+"F20.imprint","IMPRINT",EDGE,{"disambiguationData":[TD([[makeQuery(id+"F20.imprint","INTERSECT",VERTEX,{"derivedFrom":[subQ0,sQuery(id+"F20.wireOp",EDGE,"E89.MirrorCS")]}),1.0]])],"derivedFrom":subQ0})])]})]});}
            var Q7;
            {var subQ0=sQuery(id+"F20.wireOp",EDGE,"E89.MirrorCS");var subQ1=sQuery(id+"F20.wireOp",EDGE,"E73");Q7=makeQuery(id+"F23.opFillet","BLEND_EDGE",EDGE,{"blendedFrom":[makeQuery(id+"F21.opRevolve","SWEPT_EDGE",EDGE,{"disambiguationData":[OSD([subQ1,subQ0])]}),makeQuery(id+"F21.opRevolve","CAP_FACE",FACE,{"disambiguationData":[OSD([subQ1,sQuery(id+"F20.wireOp",EDGE,"E74"),subQ0,sQuery(id+"F20.wireOp",EDGE,"E90.MirrorCS")])],"isStart":true})],"blendedInto":[makeQuery(id+"F21.opRevolve","CAP_FACE",FACE,{"disambiguationData":[OSD([subQ1,sQuery(id+"F20.wireOp",EDGE,"E74"),subQ0,sQuery(id+"F20.wireOp",EDGE,"E90.MirrorCS")])],"isStart":true})]});}
            var Q8;
            {var subQ0=sQuery(id+"F20.wireOp",EDGE,"E73");var subQ1=sQuery(id+"F20.wireOp",EDGE,"E92.MirrorCS");Q8=makeQuery(id+"F24.opFillet","BLEND_EDGE",EDGE,{"blendedFrom":[makeQuery(id+"F21.opRevolve","CAP_EDGE",EDGE,{"disambiguationData":[OSD([subQ1])],"isStart":true}),makeQuery(id+"F21.opRevolve","SWEPT_FACE",FACE,{"disambiguationData":[OSD([subQ0]),TDD([makeQuery(id+"F20.imprint","IMPRINT",EDGE,{"disambiguationData":[TD([[makeQuery(id+"F20.imprint","INTERSECT",VERTEX,{"derivedFrom":[subQ0,sQuery(id+"F20.wireOp",EDGE,"E91.MirrorCS")]}),1.0]])],"derivedFrom":subQ0})])]})],"blendedInto":[makeQuery(id+"F21.opRevolve","SWEPT_FACE",FACE,{"disambiguationData":[OSD([subQ0]),TDD([makeQuery(id+"F20.imprint","IMPRINT",EDGE,{"disambiguationData":[TD([[makeQuery(id+"F20.imprint","INTERSECT",VERTEX,{"derivedFrom":[subQ0,sQuery(id+"F20.wireOp",EDGE,"E91.MirrorCS")]}),1.0]])],"derivedFrom":subQ0})])]})]});}
            var Q9;
            {var subQ0=sQuery(id+"F20.wireOp",EDGE,"E91.MirrorCS");var subQ1=sQuery(id+"F20.wireOp",EDGE,"E73");Q9=makeQuery(id+"F23.opFillet","BLEND_EDGE",EDGE,{"blendedFrom":[makeQuery(id+"F21.opRevolve","SWEPT_EDGE",EDGE,{"disambiguationData":[OSD([subQ1,subQ0])]}),makeQuery(id+"F21.opRevolve","CAP_FACE",FACE,{"disambiguationData":[OSD([subQ1,sQuery(id+"F20.wireOp",EDGE,"E74"),subQ0,sQuery(id+"F20.wireOp",EDGE,"E92.MirrorCS")])],"isStart":true})],"blendedInto":[makeQuery(id+"F21.opRevolve","CAP_FACE",FACE,{"disambiguationData":[OSD([subQ1,sQuery(id+"F20.wireOp",EDGE,"E74"),subQ0,sQuery(id+"F20.wireOp",EDGE,"E92.MirrorCS")])],"isStart":true})]});}
            fillet(context, id + "F25", {"entities" : qUnion([Q0, Q1, Q2, Q3, Q4, Q5, Q6, Q7, Q8, Q9]), "radius" : 2 * mm, "tangentPropagation" : true, "allowEdgeOverflow" : false});
        }
        {
            var Q0;
            Q0=makeQuery(id+"F21.opRevolve","SWEPT_BODY",BODY,{"disambiguationData":[OSD([sQuery(id+"F20.wireOp",EDGE,"E73"),sQuery(id+"F20.wireOp",EDGE,"E74"),sQuery(id+"F20.wireOp",EDGE,"E91.MirrorCS"),sQuery(id+"F20.wireOp",EDGE,"E92.MirrorCS")])]});
            var Q1;
            Q1=makeQuery(id+"F21.opRevolve","SWEPT_BODY",BODY,{"disambiguationData":[OSD([sQuery(id+"F20.wireOp",EDGE,"E73"),sQuery(id+"F20.wireOp",EDGE,"E74"),sQuery(id+"F20.wireOp",EDGE,"E89.MirrorCS"),sQuery(id+"F20.wireOp",EDGE,"E90.MirrorCS")])]});
            var Q2;
            Q2=makeQuery(id+"F21.opRevolve","SWEPT_BODY",BODY,{"disambiguationData":[OSD([sQuery(id+"F20.wireOp",EDGE,"E73"),sQuery(id+"F20.wireOp",EDGE,"E74"),sQuery(id+"F20.wireOp",EDGE,"E76"),sQuery(id+"F20.wireOp",EDGE,"E88.MirrorCS")])]});
            var Q3;
            Q3=makeQuery(id+"F21.opRevolve","SWEPT_BODY",BODY,{"disambiguationData":[OSD([sQuery(id+"F20.wireOp",EDGE,"E73"),sQuery(id+"F20.wireOp",EDGE,"E74"),sQuery(id+"F20.wireOp",EDGE,"E77"),sQuery(id+"F20.wireOp",EDGE,"E78")])]});
            var Q4;
            Q4=makeQuery(id+"F21.opRevolve","SWEPT_BODY",BODY,{"disambiguationData":[OSD([sQuery(id+"F20.wireOp",EDGE,"E73"),sQuery(id+"F20.wireOp",EDGE,"E74"),sQuery(id+"F20.wireOp",EDGE,"E79"),sQuery(id+"F20.wireOp",EDGE,"E81")])]});
            var Q5;
            Q5=sQuery(id+"F2.wireOp",EDGE,"E35");
            transform(context, id + "F26", {"entities" : qUnion([Q0, Q1, Q2, Q3, Q4]), "transformType" : TransformType.ROTATION, "transformAxis" : qUnion([Q5]), "angle" : 30 * degree, "makeCopy" : true});
        }
        {
            var Q0;
            Q0=makeQuery(id+"F26.opPattern","COPY",BODY,{"derivedFrom":makeQuery(id+"F21.opRevolve","SWEPT_BODY",BODY,{"disambiguationData":[OSD([sQuery(id+"F20.wireOp",EDGE,"E73"),sQuery(id+"F20.wireOp",EDGE,"E74"),sQuery(id+"F20.wireOp",EDGE,"E79"),sQuery(id+"F20.wireOp",EDGE,"E81")])]}),"instanceName":"1"});
            var Q1;
            Q1=makeQuery(id+"F26.opPattern","COPY",BODY,{"derivedFrom":makeQuery(id+"F21.opRevolve","SWEPT_BODY",BODY,{"disambiguationData":[OSD([sQuery(id+"F20.wireOp",EDGE,"E73"),sQuery(id+"F20.wireOp",EDGE,"E74"),sQuery(id+"F20.wireOp",EDGE,"E77"),sQuery(id+"F20.wireOp",EDGE,"E78")])]}),"instanceName":"1"});
            var Q2;
            Q2=makeQuery(id+"F26.opPattern","COPY",BODY,{"derivedFrom":makeQuery(id+"F21.opRevolve","SWEPT_BODY",BODY,{"disambiguationData":[OSD([sQuery(id+"F20.wireOp",EDGE,"E73"),sQuery(id+"F20.wireOp",EDGE,"E74"),sQuery(id+"F20.wireOp",EDGE,"E76"),sQuery(id+"F20.wireOp",EDGE,"E88.MirrorCS")])]}),"instanceName":"1"});
            var Q3;
            Q3=makeQuery(id+"F26.opPattern","COPY",BODY,{"derivedFrom":makeQuery(id+"F21.opRevolve","SWEPT_BODY",BODY,{"disambiguationData":[OSD([sQuery(id+"F20.wireOp",EDGE,"E73"),sQuery(id+"F20.wireOp",EDGE,"E74"),sQuery(id+"F20.wireOp",EDGE,"E89.MirrorCS"),sQuery(id+"F20.wireOp",EDGE,"E90.MirrorCS")])]}),"instanceName":"1"});
            var Q4;
            Q4=makeQuery(id+"F26.opPattern","COPY",BODY,{"derivedFrom":makeQuery(id+"F21.opRevolve","SWEPT_BODY",BODY,{"disambiguationData":[OSD([sQuery(id+"F20.wireOp",EDGE,"E73"),sQuery(id+"F20.wireOp",EDGE,"E74"),sQuery(id+"F20.wireOp",EDGE,"E91.MirrorCS"),sQuery(id+"F20.wireOp",EDGE,"E92.MirrorCS")])]}),"instanceName":"1"});
            var Q5;
            Q5=sQuery(id+"F2.wireOp",EDGE,"E35");
            circularPattern(context, id + "F27", {"entities" : qUnion([Q0, Q1, Q2, Q3, Q4]), "axis" : qUnion([Q5]), "angle" : 180 * degree, "instanceCount" : 2});
        }
        {
            var Q0;
            Q0=makeQuery(id+"F26.opPattern","COPY",BODY,{"derivedFrom":makeQuery(id+"F21.opRevolve","SWEPT_BODY",BODY,{"disambiguationData":[OSD([sQuery(id+"F20.wireOp",EDGE,"E73"),sQuery(id+"F20.wireOp",EDGE,"E74"),sQuery(id+"F20.wireOp",EDGE,"E79"),sQuery(id+"F20.wireOp",EDGE,"E81")])]}),"instanceName":"1"});
            var Q1;
            Q1=makeQuery(id+"F26.opPattern","COPY",BODY,{"derivedFrom":makeQuery(id+"F21.opRevolve","SWEPT_BODY",BODY,{"disambiguationData":[OSD([sQuery(id+"F20.wireOp",EDGE,"E73"),sQuery(id+"F20.wireOp",EDGE,"E74"),sQuery(id+"F20.wireOp",EDGE,"E77"),sQuery(id+"F20.wireOp",EDGE,"E78")])]}),"instanceName":"1"});
            var Q2;
            Q2=makeQuery(id+"F26.opPattern","COPY",BODY,{"derivedFrom":makeQuery(id+"F21.opRevolve","SWEPT_BODY",BODY,{"disambiguationData":[OSD([sQuery(id+"F20.wireOp",EDGE,"E73"),sQuery(id+"F20.wireOp",EDGE,"E74"),sQuery(id+"F20.wireOp",EDGE,"E76"),sQuery(id+"F20.wireOp",EDGE,"E88.MirrorCS")])]}),"instanceName":"1"});
            var Q3;
            Q3=makeQuery(id+"F26.opPattern","COPY",BODY,{"derivedFrom":makeQuery(id+"F21.opRevolve","SWEPT_BODY",BODY,{"disambiguationData":[OSD([sQuery(id+"F20.wireOp",EDGE,"E73"),sQuery(id+"F20.wireOp",EDGE,"E74"),sQuery(id+"F20.wireOp",EDGE,"E89.MirrorCS"),sQuery(id+"F20.wireOp",EDGE,"E90.MirrorCS")])]}),"instanceName":"1"});
            var Q4;
            Q4=makeQuery(id+"F26.opPattern","COPY",BODY,{"derivedFrom":makeQuery(id+"F21.opRevolve","SWEPT_BODY",BODY,{"disambiguationData":[OSD([sQuery(id+"F20.wireOp",EDGE,"E73"),sQuery(id+"F20.wireOp",EDGE,"E74"),sQuery(id+"F20.wireOp",EDGE,"E91.MirrorCS"),sQuery(id+"F20.wireOp",EDGE,"E92.MirrorCS")])]}),"instanceName":"1"});
            var Q5;
            Q5=makeQuery(id+"F27.opPattern","COPY",BODY,{"derivedFrom":makeQuery(id+"F26.opPattern","COPY",BODY,{"derivedFrom":makeQuery(id+"F21.opRevolve","SWEPT_BODY",BODY,{"disambiguationData":[OSD([sQuery(id+"F20.wireOp",EDGE,"E73"),sQuery(id+"F20.wireOp",EDGE,"E74"),sQuery(id+"F20.wireOp",EDGE,"E91.MirrorCS"),sQuery(id+"F20.wireOp",EDGE,"E92.MirrorCS")])]}),"instanceName":"1"}),"instanceName":"1"});
            var Q6;
            Q6=makeQuery(id+"F27.opPattern","COPY",BODY,{"derivedFrom":makeQuery(id+"F26.opPattern","COPY",BODY,{"derivedFrom":makeQuery(id+"F21.opRevolve","SWEPT_BODY",BODY,{"disambiguationData":[OSD([sQuery(id+"F20.wireOp",EDGE,"E73"),sQuery(id+"F20.wireOp",EDGE,"E74"),sQuery(id+"F20.wireOp",EDGE,"E89.MirrorCS"),sQuery(id+"F20.wireOp",EDGE,"E90.MirrorCS")])]}),"instanceName":"1"}),"instanceName":"1"});
            var Q7;
            Q7=makeQuery(id+"F27.opPattern","COPY",BODY,{"derivedFrom":makeQuery(id+"F26.opPattern","COPY",BODY,{"derivedFrom":makeQuery(id+"F21.opRevolve","SWEPT_BODY",BODY,{"disambiguationData":[OSD([sQuery(id+"F20.wireOp",EDGE,"E73"),sQuery(id+"F20.wireOp",EDGE,"E74"),sQuery(id+"F20.wireOp",EDGE,"E76"),sQuery(id+"F20.wireOp",EDGE,"E88.MirrorCS")])]}),"instanceName":"1"}),"instanceName":"1"});
            var Q8;
            Q8=makeQuery(id+"F27.opPattern","COPY",BODY,{"derivedFrom":makeQuery(id+"F26.opPattern","COPY",BODY,{"derivedFrom":makeQuery(id+"F21.opRevolve","SWEPT_BODY",BODY,{"disambiguationData":[OSD([sQuery(id+"F20.wireOp",EDGE,"E73"),sQuery(id+"F20.wireOp",EDGE,"E74"),sQuery(id+"F20.wireOp",EDGE,"E77"),sQuery(id+"F20.wireOp",EDGE,"E78")])]}),"instanceName":"1"}),"instanceName":"1"});
            var Q9;
            Q9=makeQuery(id+"F27.opPattern","COPY",BODY,{"derivedFrom":makeQuery(id+"F26.opPattern","COPY",BODY,{"derivedFrom":makeQuery(id+"F21.opRevolve","SWEPT_BODY",BODY,{"disambiguationData":[OSD([sQuery(id+"F20.wireOp",EDGE,"E73"),sQuery(id+"F20.wireOp",EDGE,"E74"),sQuery(id+"F20.wireOp",EDGE,"E79"),sQuery(id+"F20.wireOp",EDGE,"E81")])]}),"instanceName":"1"}),"instanceName":"1"});
            var Q10;
            Q10=makeQuery(id+"F1.opExtrude","SWEPT_BODY",BODY,{"disambiguationData":[OSD([sQuery(id+"F0.wireOp",EDGE,"E9.rect.bottom"),sQuery(id+"F0.wireOp",EDGE,"E9.rect.top"),sQuery(id+"F0.wireOp",EDGE,"E9.rect.left"),sQuery(id+"F0.wireOp",EDGE,"E9.rect.right"),sQuery(id+"F0.wireOp",EDGE,"E10"),sQuery(id+"F0.wireOp",EDGE,"E11"),sQuery(id+"F0.wireOp",EDGE,"E13"),sQuery(id+"F0.wireOp",EDGE,"E15.MirrorCS"),sQuery(id+"F0.wireOp",EDGE,"E16.MirrorCS"),sQuery(id+"F0.wireOp",EDGE,"E17.MirrorCS"),sQuery(id+"F0.wireOp",EDGE,"E18.MirrorCS"),sQuery(id+"F0.wireOp",EDGE,"E19.MirrorCS"),sQuery(id+"F0.wireOp",EDGE,"E20.MirrorCS"),sQuery(id+"F0.wireOp",EDGE,"E28"),sQuery(id+"F0.wireOp",EDGE,"E29.MirrorC")])]});
            booleanBodies(context, id + "F28", {"operationType" : BooleanOperationType.SUBTRACTION, "tools" : qUnion([Q0, Q1, Q2, Q3, Q4, Q5, Q6, Q7, Q8, Q9]), "targets" : qUnion([Q10])});
        }
        {
            var Q0;
            Q0=makeQuery(id+"F21.opRevolve","SWEPT_BODY",BODY,{"disambiguationData":[OSD([sQuery(id+"F20.wireOp",EDGE,"E73"),sQuery(id+"F20.wireOp",EDGE,"E74"),sQuery(id+"F20.wireOp",EDGE,"E91.MirrorCS"),sQuery(id+"F20.wireOp",EDGE,"E92.MirrorCS")])]});
            var Q1;
            Q1=makeQuery(id+"F21.opRevolve","SWEPT_BODY",BODY,{"disambiguationData":[OSD([sQuery(id+"F20.wireOp",EDGE,"E73"),sQuery(id+"F20.wireOp",EDGE,"E74"),sQuery(id+"F20.wireOp",EDGE,"E89.MirrorCS"),sQuery(id+"F20.wireOp",EDGE,"E90.MirrorCS")])]});
            var Q2;
            Q2=makeQuery(id+"F21.opRevolve","SWEPT_BODY",BODY,{"disambiguationData":[OSD([sQuery(id+"F20.wireOp",EDGE,"E73"),sQuery(id+"F20.wireOp",EDGE,"E74"),sQuery(id+"F20.wireOp",EDGE,"E76"),sQuery(id+"F20.wireOp",EDGE,"E88.MirrorCS")])]});
            var Q3;
            Q3=makeQuery(id+"F21.opRevolve","SWEPT_BODY",BODY,{"disambiguationData":[OSD([sQuery(id+"F20.wireOp",EDGE,"E73"),sQuery(id+"F20.wireOp",EDGE,"E74"),sQuery(id+"F20.wireOp",EDGE,"E77"),sQuery(id+"F20.wireOp",EDGE,"E78")])]});
            var Q4;
            Q4=makeQuery(id+"F21.opRevolve","SWEPT_BODY",BODY,{"disambiguationData":[OSD([sQuery(id+"F20.wireOp",EDGE,"E73"),sQuery(id+"F20.wireOp",EDGE,"E74"),sQuery(id+"F20.wireOp",EDGE,"E79"),sQuery(id+"F20.wireOp",EDGE,"E81")])]});
            var Q5;
            Q5=sQuery(id+"F2.wireOp",EDGE,"E35");
            transform(context, id + "F29", {"entities" : qUnion([Q0, Q1, Q2, Q3, Q4]), "transformType" : TransformType.ROTATION, "transformAxis" : qUnion([Q5]), "angle" : 30 * degree, "oppositeDirection" : true, "makeCopy" : true});
        }
        {
            var Q0;
            Q0=makeQuery(id+"F29.opPattern","COPY",BODY,{"derivedFrom":makeQuery(id+"F21.opRevolve","SWEPT_BODY",BODY,{"disambiguationData":[OSD([sQuery(id+"F20.wireOp",EDGE,"E73"),sQuery(id+"F20.wireOp",EDGE,"E74"),sQuery(id+"F20.wireOp",EDGE,"E91.MirrorCS"),sQuery(id+"F20.wireOp",EDGE,"E92.MirrorCS")])]}),"instanceName":"1"});
            var Q1;
            Q1=makeQuery(id+"F29.opPattern","COPY",BODY,{"derivedFrom":makeQuery(id+"F21.opRevolve","SWEPT_BODY",BODY,{"disambiguationData":[OSD([sQuery(id+"F20.wireOp",EDGE,"E73"),sQuery(id+"F20.wireOp",EDGE,"E74"),sQuery(id+"F20.wireOp",EDGE,"E89.MirrorCS"),sQuery(id+"F20.wireOp",EDGE,"E90.MirrorCS")])]}),"instanceName":"1"});
            var Q2;
            Q2=makeQuery(id+"F29.opPattern","COPY",BODY,{"derivedFrom":makeQuery(id+"F21.opRevolve","SWEPT_BODY",BODY,{"disambiguationData":[OSD([sQuery(id+"F20.wireOp",EDGE,"E73"),sQuery(id+"F20.wireOp",EDGE,"E74"),sQuery(id+"F20.wireOp",EDGE,"E76"),sQuery(id+"F20.wireOp",EDGE,"E88.MirrorCS")])]}),"instanceName":"1"});
            var Q3;
            Q3=makeQuery(id+"F29.opPattern","COPY",BODY,{"derivedFrom":makeQuery(id+"F21.opRevolve","SWEPT_BODY",BODY,{"disambiguationData":[OSD([sQuery(id+"F20.wireOp",EDGE,"E73"),sQuery(id+"F20.wireOp",EDGE,"E74"),sQuery(id+"F20.wireOp",EDGE,"E77"),sQuery(id+"F20.wireOp",EDGE,"E78")])]}),"instanceName":"1"});
            var Q4;
            Q4=makeQuery(id+"F29.opPattern","COPY",BODY,{"derivedFrom":makeQuery(id+"F21.opRevolve","SWEPT_BODY",BODY,{"disambiguationData":[OSD([sQuery(id+"F20.wireOp",EDGE,"E73"),sQuery(id+"F20.wireOp",EDGE,"E74"),sQuery(id+"F20.wireOp",EDGE,"E79"),sQuery(id+"F20.wireOp",EDGE,"E81")])]}),"instanceName":"1"});
            var Q5;
            Q5=sQuery(id+"F2.wireOp",EDGE,"E35");
            circularPattern(context, id + "F30", {"entities" : qUnion([Q0, Q1, Q2, Q3, Q4]), "axis" : qUnion([Q5]), "angle" : 180 * degree, "instanceCount" : 2});
        }
        {
            var Q0;
            Q0=makeQuery(id+"F29.opPattern","COPY",BODY,{"derivedFrom":makeQuery(id+"F21.opRevolve","SWEPT_BODY",BODY,{"disambiguationData":[OSD([sQuery(id+"F20.wireOp",EDGE,"E73"),sQuery(id+"F20.wireOp",EDGE,"E74"),sQuery(id+"F20.wireOp",EDGE,"E91.MirrorCS"),sQuery(id+"F20.wireOp",EDGE,"E92.MirrorCS")])]}),"instanceName":"1"});
            var Q1;
            Q1=makeQuery(id+"F29.opPattern","COPY",BODY,{"derivedFrom":makeQuery(id+"F21.opRevolve","SWEPT_BODY",BODY,{"disambiguationData":[OSD([sQuery(id+"F20.wireOp",EDGE,"E73"),sQuery(id+"F20.wireOp",EDGE,"E74"),sQuery(id+"F20.wireOp",EDGE,"E89.MirrorCS"),sQuery(id+"F20.wireOp",EDGE,"E90.MirrorCS")])]}),"instanceName":"1"});
            var Q2;
            Q2=makeQuery(id+"F29.opPattern","COPY",BODY,{"derivedFrom":makeQuery(id+"F21.opRevolve","SWEPT_BODY",BODY,{"disambiguationData":[OSD([sQuery(id+"F20.wireOp",EDGE,"E73"),sQuery(id+"F20.wireOp",EDGE,"E74"),sQuery(id+"F20.wireOp",EDGE,"E76"),sQuery(id+"F20.wireOp",EDGE,"E88.MirrorCS")])]}),"instanceName":"1"});
            var Q3;
            Q3=makeQuery(id+"F29.opPattern","COPY",BODY,{"derivedFrom":makeQuery(id+"F21.opRevolve","SWEPT_BODY",BODY,{"disambiguationData":[OSD([sQuery(id+"F20.wireOp",EDGE,"E73"),sQuery(id+"F20.wireOp",EDGE,"E74"),sQuery(id+"F20.wireOp",EDGE,"E77"),sQuery(id+"F20.wireOp",EDGE,"E78")])]}),"instanceName":"1"});
            var Q4;
            Q4=makeQuery(id+"F29.opPattern","COPY",BODY,{"derivedFrom":makeQuery(id+"F21.opRevolve","SWEPT_BODY",BODY,{"disambiguationData":[OSD([sQuery(id+"F20.wireOp",EDGE,"E73"),sQuery(id+"F20.wireOp",EDGE,"E74"),sQuery(id+"F20.wireOp",EDGE,"E79"),sQuery(id+"F20.wireOp",EDGE,"E81")])]}),"instanceName":"1"});
            var Q5;
            Q5=makeQuery(id+"F30.opPattern","COPY",BODY,{"derivedFrom":makeQuery(id+"F29.opPattern","COPY",BODY,{"derivedFrom":makeQuery(id+"F21.opRevolve","SWEPT_BODY",BODY,{"disambiguationData":[OSD([sQuery(id+"F20.wireOp",EDGE,"E73"),sQuery(id+"F20.wireOp",EDGE,"E74"),sQuery(id+"F20.wireOp",EDGE,"E91.MirrorCS"),sQuery(id+"F20.wireOp",EDGE,"E92.MirrorCS")])]}),"instanceName":"1"}),"instanceName":"1"});
            var Q6;
            Q6=makeQuery(id+"F30.opPattern","COPY",BODY,{"derivedFrom":makeQuery(id+"F29.opPattern","COPY",BODY,{"derivedFrom":makeQuery(id+"F21.opRevolve","SWEPT_BODY",BODY,{"disambiguationData":[OSD([sQuery(id+"F20.wireOp",EDGE,"E73"),sQuery(id+"F20.wireOp",EDGE,"E74"),sQuery(id+"F20.wireOp",EDGE,"E89.MirrorCS"),sQuery(id+"F20.wireOp",EDGE,"E90.MirrorCS")])]}),"instanceName":"1"}),"instanceName":"1"});
            var Q7;
            Q7=makeQuery(id+"F30.opPattern","COPY",BODY,{"derivedFrom":makeQuery(id+"F29.opPattern","COPY",BODY,{"derivedFrom":makeQuery(id+"F21.opRevolve","SWEPT_BODY",BODY,{"disambiguationData":[OSD([sQuery(id+"F20.wireOp",EDGE,"E73"),sQuery(id+"F20.wireOp",EDGE,"E74"),sQuery(id+"F20.wireOp",EDGE,"E76"),sQuery(id+"F20.wireOp",EDGE,"E88.MirrorCS")])]}),"instanceName":"1"}),"instanceName":"1"});
            var Q8;
            Q8=makeQuery(id+"F30.opPattern","COPY",BODY,{"derivedFrom":makeQuery(id+"F29.opPattern","COPY",BODY,{"derivedFrom":makeQuery(id+"F21.opRevolve","SWEPT_BODY",BODY,{"disambiguationData":[OSD([sQuery(id+"F20.wireOp",EDGE,"E73"),sQuery(id+"F20.wireOp",EDGE,"E74"),sQuery(id+"F20.wireOp",EDGE,"E77"),sQuery(id+"F20.wireOp",EDGE,"E78")])]}),"instanceName":"1"}),"instanceName":"1"});
            var Q9;
            Q9=makeQuery(id+"F30.opPattern","COPY",BODY,{"derivedFrom":makeQuery(id+"F29.opPattern","COPY",BODY,{"derivedFrom":makeQuery(id+"F21.opRevolve","SWEPT_BODY",BODY,{"disambiguationData":[OSD([sQuery(id+"F20.wireOp",EDGE,"E73"),sQuery(id+"F20.wireOp",EDGE,"E74"),sQuery(id+"F20.wireOp",EDGE,"E79"),sQuery(id+"F20.wireOp",EDGE,"E81")])]}),"instanceName":"1"}),"instanceName":"1"});
            var Q10;
            Q10=makeQuery(id+"F1.opExtrude","SWEPT_BODY",BODY,{"disambiguationData":[OSD([sQuery(id+"F0.wireOp",EDGE,"E9.rect.bottom"),sQuery(id+"F0.wireOp",EDGE,"E9.rect.top"),sQuery(id+"F0.wireOp",EDGE,"E9.rect.left"),sQuery(id+"F0.wireOp",EDGE,"E9.rect.right"),sQuery(id+"F0.wireOp",EDGE,"E10"),sQuery(id+"F0.wireOp",EDGE,"E11"),sQuery(id+"F0.wireOp",EDGE,"E13"),sQuery(id+"F0.wireOp",EDGE,"E15.MirrorCS"),sQuery(id+"F0.wireOp",EDGE,"E16.MirrorCS"),sQuery(id+"F0.wireOp",EDGE,"E17.MirrorCS"),sQuery(id+"F0.wireOp",EDGE,"E18.MirrorCS"),sQuery(id+"F0.wireOp",EDGE,"E19.MirrorCS"),sQuery(id+"F0.wireOp",EDGE,"E20.MirrorCS"),sQuery(id+"F0.wireOp",EDGE,"E28"),sQuery(id+"F0.wireOp",EDGE,"E29.MirrorC")])]});
            booleanBodies(context, id + "F31", {"operationType" : BooleanOperationType.SUBTRACTION, "tools" : qUnion([Q0, Q1, Q2, Q3, Q4, Q5, Q6, Q7, Q8, Q9]), "targets" : qUnion([Q10])});
        }
        {
            var Q0;
            Q0=makeQuery(id+"F18.opExtrude","CAP_FACE",FACE,{"disambiguationData":[OSD([sQuery(id+"F17.wireOp",EDGE,"E47"),sQuery(id+"F17.wireOp",EDGE,"E48"),sQuery(id+"F17.wireOp",EDGE,"E51"),sQuery(id+"F17.wireOp",EDGE,"E52"),sQuery(id+"F17.wireOp",EDGE,"E53"),sQuery(id+"F17.wireOp",EDGE,"E54"),sQuery(id+"F17.wireOp",EDGE,"E55"),sQuery(id+"F17.wireOp",EDGE,"E57"),sQuery(id+"F17.wireOp",EDGE,"E58"),sQuery(id+"F17.wireOp",EDGE,"E59"),sQuery(id+"F17.wireOp",EDGE,"E60"),sQuery(id+"F17.wireOp",EDGE,"E62.MirrorCS"),sQuery(id+"F17.wireOp",EDGE,"E63.MirrorCS"),sQuery(id+"F17.wireOp",EDGE,"E64.MirrorC"),sQuery(id+"F17.wireOp",EDGE,"E65.MirrorC"),sQuery(id+"F17.wireOp",EDGE,"E66.MirrorCS"),sQuery(id+"F17.wireOp",EDGE,"E67.MirrorCS"),sQuery(id+"F17.wireOp",EDGE,"E68.MirrorCS"),sQuery(id+"F17.wireOp",EDGE,"E69.MirrorCS"),sQuery(id+"F17.wireOp",EDGE,"E70.MirrorCS"),sQuery(id+"F17.wireOp",EDGE,"E71.MirrorCS"),sQuery(id+"F17.wireOp",EDGE,"E72")])],"isStart":true});
            var sketch = newSketch(context, id + "F32", { "sketchPlane" : qUnion([Q0])});
            skLineSegment(sketch, "E93", {"start": v(-71.63, 29.58) * mm, "end": v(-70.89, 35.53) * mm});
            skLineSegment(sketch, "E94", {"start": v(-70.89, 35.53) * mm, "end": v(-64.38, 31.22) * mm});
            skLineSegment(sketch, "E95", {"start": v(-64.38, 31.22) * mm, "end": v(-64.38, 25.4) * mm});
            skLineSegment(sketch, "E96", {"start": v(-64.38, 25.4) * mm, "end": v(-71.63, 29.58) * mm});
            skSolve(sketch);
        }
        {
            var Q0;
            Q0=makeQuery(id+"F32.imprint","IMPRINT",FACE,{"disambiguationData":[TD([[makeQuery(id+"F32.imprint","IMPRINT",EDGE,{"derivedFrom":sQuery(id+"F32.wireOp",EDGE,"E93")}),1.0]])]});
            extrude(context, id + "F33", {"entities" : qUnion([Q0]), "operationType" : NewBodyOperationType.REMOVE, "oppositeDirection" : true, "depth" : 5 * mm});
        }
    });
